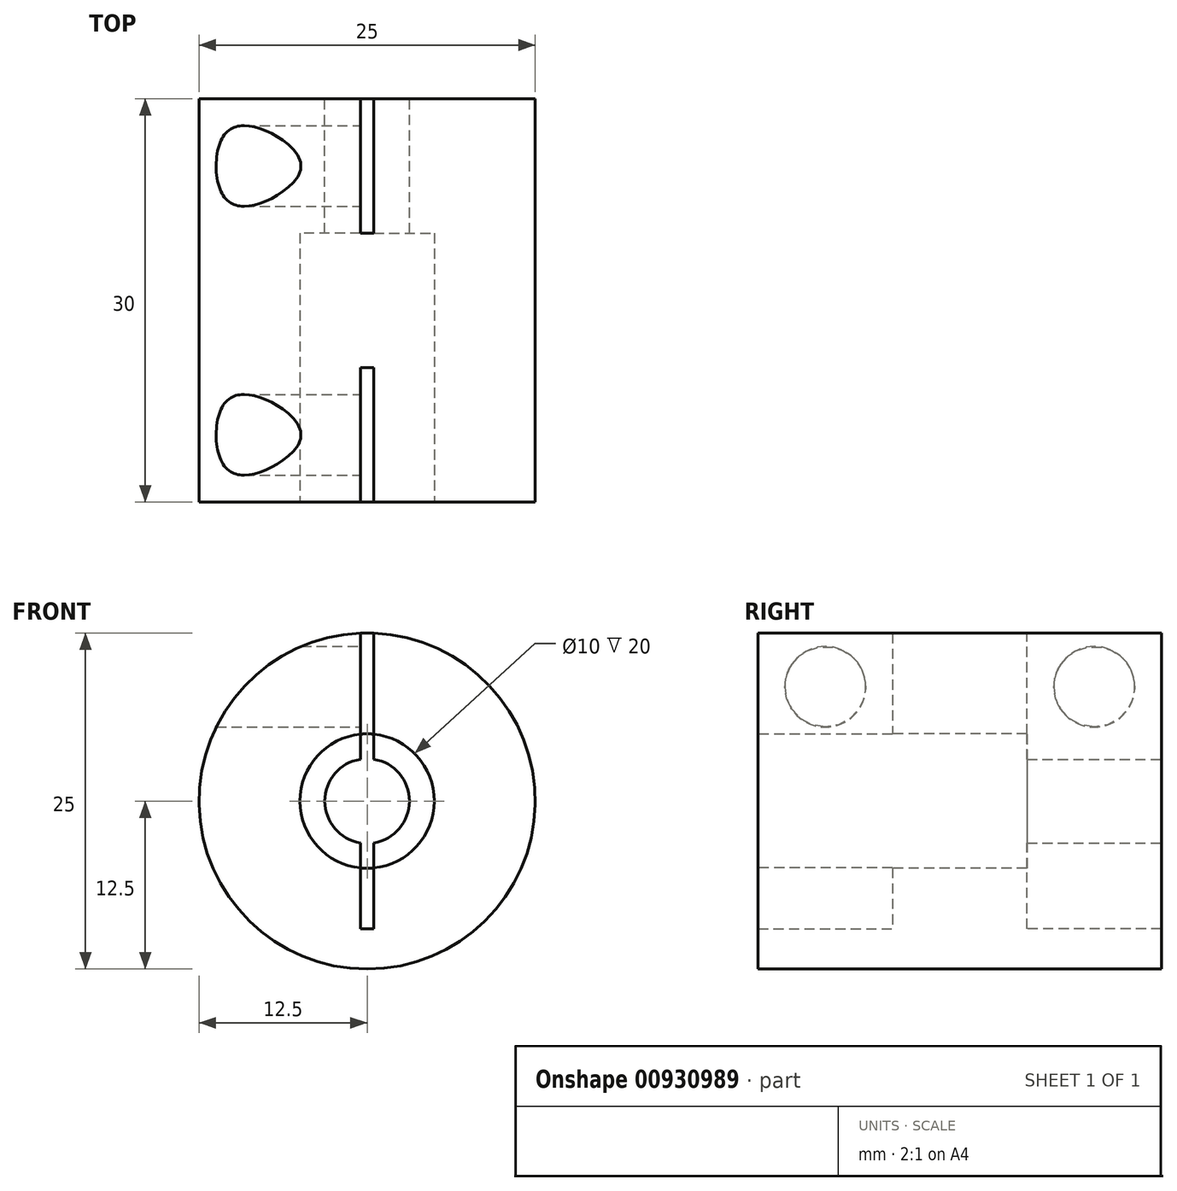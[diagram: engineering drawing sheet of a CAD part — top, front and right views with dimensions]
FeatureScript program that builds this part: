
annotation { "Feature Type Name" : "Feature", "Feature Type Description" : "" }
export const myFeature = defineFeature(function(context is Context, id is Id, definition is map)
    precondition{}
    {
        {
            var Q0;
            Q0=qCreatedBy(makeId("Front.planeOp"),FACE);
            var sketch = newSketch(context, id + "F0", { "sketchPlane" : qUnion([Q0])});
            skCircle(sketch, "E0", {"center": v(0, 0) * mm, "radius": 12.5 * mm});
            skSolve(sketch);
        }
        {
            var Q0;
            Q0=makeQuery(id+"F0.imprint","IMPRINT",FACE,{"disambiguationData":[TD([[makeQuery(id+"F0.imprint","IMPRINT",EDGE,{"derivedFrom":sQuery(id+"F0.wireOp",EDGE,"E0")}),1.0]])]});
            extrude(context, id + "F1", {"entities" : qUnion([Q0]), "oppositeDirection" : true, "depth" : 30 * mm, "offsetDistance" : 25 * mm});
        }
        {
            var Q0;
            Q0=makeQuery(id+"F1.opExtrude","CAP_FACE",FACE,{"disambiguationData":[OSD([sQuery(id+"F0.wireOp",EDGE,"E0")])],"isStart":true});
            var sketch = newSketch(context, id + "F2", { "sketchPlane" : qUnion([Q0])});
            skCircle(sketch, "E1", {"center": v(0, 0) * mm, "radius": 5 * mm});
            skSolve(sketch);
        }
        {
            var Q0;
            Q0=makeQuery(id+"F2.imprint","IMPRINT",FACE,{"disambiguationData":[TD([[makeQuery(id+"F2.imprint","IMPRINT",EDGE,{"derivedFrom":sQuery(id+"F2.wireOp",EDGE,"E1")}),1.0]])]});
            extrude(context, id + "F3", {"entities" : qUnion([Q0]), "operationType" : NewBodyOperationType.REMOVE, "oppositeDirection" : true, "depth" : 20 * mm, "offsetDistance" : 25 * mm});
        }
        {
            var Q0;
            Q0=makeQuery(id+"F1.opExtrude","CAP_FACE",FACE,{"disambiguationData":[OSD([sQuery(id+"F0.wireOp",EDGE,"E0")])],"isStart":false});
            var sketch = newSketch(context, id + "F4", { "sketchPlane" : qUnion([Q0])});
            skCircle(sketch, "E2", {"center": v(0, 0) * mm, "radius": 3.15 * mm});
            skSolve(sketch);
        }
        {
            var Q0;
            Q0=makeQuery(id+"F4.imprint","IMPRINT",FACE,{"disambiguationData":[TD([[makeQuery(id+"F4.imprint","IMPRINT",EDGE,{"derivedFrom":sQuery(id+"F4.wireOp",EDGE,"E2")}),1.0]])]});
            extrude(context, id + "F5", {"entities" : qUnion([Q0]), "operationType" : NewBodyOperationType.REMOVE, "endBound" : BoundingType.UP_TO_NEXT, "oppositeDirection" : true, "depth" : 25 * mm, "offsetDistance" : 25 * mm});
        }
        {
            var Q0;
            Q0=qCreatedBy(makeId("Right.planeOp"),FACE);
            var sketch = newSketch(context, id + "F6", { "sketchPlane" : qUnion([Q0])});
            skLineSegment(sketch, "E3.bottom", {"start": v(0, 12.5) * mm, "end": v(10, 12.5) * mm});
            skLineSegment(sketch, "E3.top", {"start": v(0, -9.5) * mm, "end": v(10, -9.5) * mm});
            skLineSegment(sketch, "E3.left", {"start": v(0, 12.5) * mm, "end": v(0, -9.5) * mm});
            skLineSegment(sketch, "E3.right", {"start": v(10, 12.5) * mm, "end": v(10, -9.5) * mm});
            skLineSegment(sketch, "E4", {"start": v(10, -9.5) * mm, "end": v(30, -9.5) * mm, "construction": true});
            skLineSegment(sketch, "E5.bottom", {"start": v(30, -9.5) * mm, "end": v(20, -9.5) * mm});
            skLineSegment(sketch, "E5.top", {"start": v(30, 12.5) * mm, "end": v(20, 12.5) * mm});
            skLineSegment(sketch, "E5.left", {"start": v(30, -9.5) * mm, "end": v(30, 12.5) * mm});
            skLineSegment(sketch, "E5.right", {"start": v(20, -9.5) * mm, "end": v(20, 12.5) * mm});
            skSolve(sketch);
        }
        {
            var Q0;
            Q0 = qSketchRegion(id + "F6", true);
            extrude(context, id + "F7", {"entities" : qUnion([Q0]), "operationType" : NewBodyOperationType.REMOVE, "oppositeDirection" : true, "depth" : 0.5 * mm, "offsetDistance" : 25 * mm, "hasSecondDirection" : true, "secondDirectionOppositeDirection" : false, "secondDirectionDepth" : 0.5 * mm});
        }
        {
            var Q0;
            Q0=qCreatedBy(makeId("Right.planeOp"),FACE);
            var sketch = newSketch(context, id + "F8", { "sketchPlane" : qUnion([Q0])});
            skCircle(sketch, "E6", {"center": v(5, 8.5) * mm, "radius": 3 * mm});
            skCircle(sketch, "E7", {"center": v(25, 8.5) * mm, "radius": 3 * mm});
            skSolve(sketch);
        }
        {
            var Q0;
            Q0 = qSketchRegion(id + "F8", true);
            var Q1;
            Q1=makeQuery(id+"F1.opExtrude","SWEPT_FACE",FACE,{"disambiguationData":[OSD([sQuery(id+"F0.wireOp",EDGE,"E0")])]});
            extrude(context, id + "F9", {"entities" : qUnion([Q0]), "operationType" : NewBodyOperationType.REMOVE, "endBound" : BoundingType.THROUGH_ALL, "oppositeDirection" : true, "depth" : 25 * mm, "endBoundEntityFace" : qUnion([Q1]), "offsetDistance" : 6 * mm});
        }
    });
